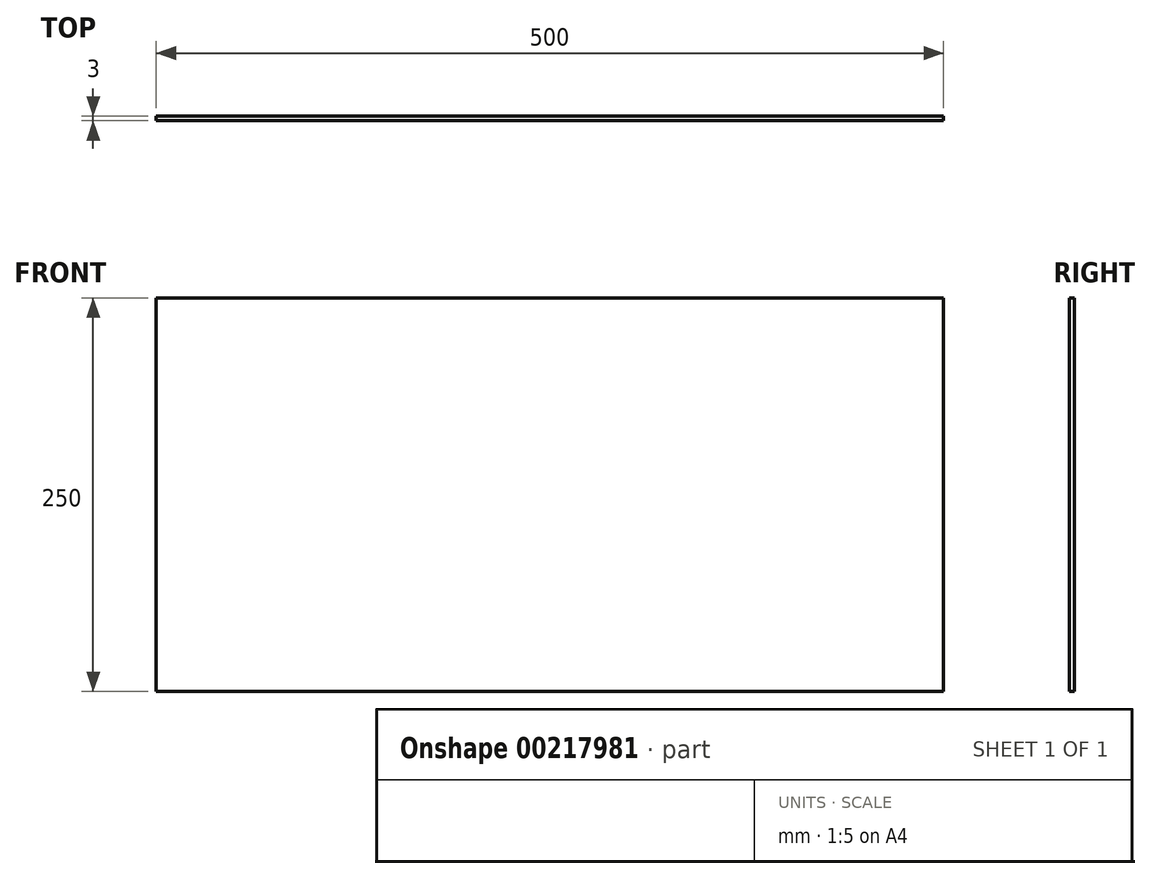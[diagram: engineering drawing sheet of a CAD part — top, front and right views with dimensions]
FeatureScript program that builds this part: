
annotation { "Feature Type Name" : "Feature", "Feature Type Description" : "" }
export const myFeature = defineFeature(function(context is Context, id is Id, definition is map)
    precondition{}
    {
        {
            var Q0;
            Q0=qCreatedBy(makeId("Front.planeOp"),FACE);
            var sketch = newSketch(context, id + "F0", { "sketchPlane" : qUnion([Q0])});
            skLineSegment(sketch, "E0.bottom", {"start": v(250, 125) * mm, "end": v(-250, 125) * mm});
            skLineSegment(sketch, "E0.top", {"start": v(250, -125) * mm, "end": v(-250, -125) * mm});
            skLineSegment(sketch, "E0.left", {"start": v(250, 125) * mm, "end": v(250, -125) * mm});
            skLineSegment(sketch, "E0.right", {"start": v(-250, 125) * mm, "end": v(-250, -125) * mm});
            skPoint(sketch, "E0.middle", {"position": v(0, 0) * mm});
            skSolve(sketch);
        }
        {
            var Q0;
            Q0 = qSketchRegion(id + "F0", true);
            extrude(context, id + "F1", {"entities" : qUnion([Q0]), "depth" : 3 * mm});
        }
    });
